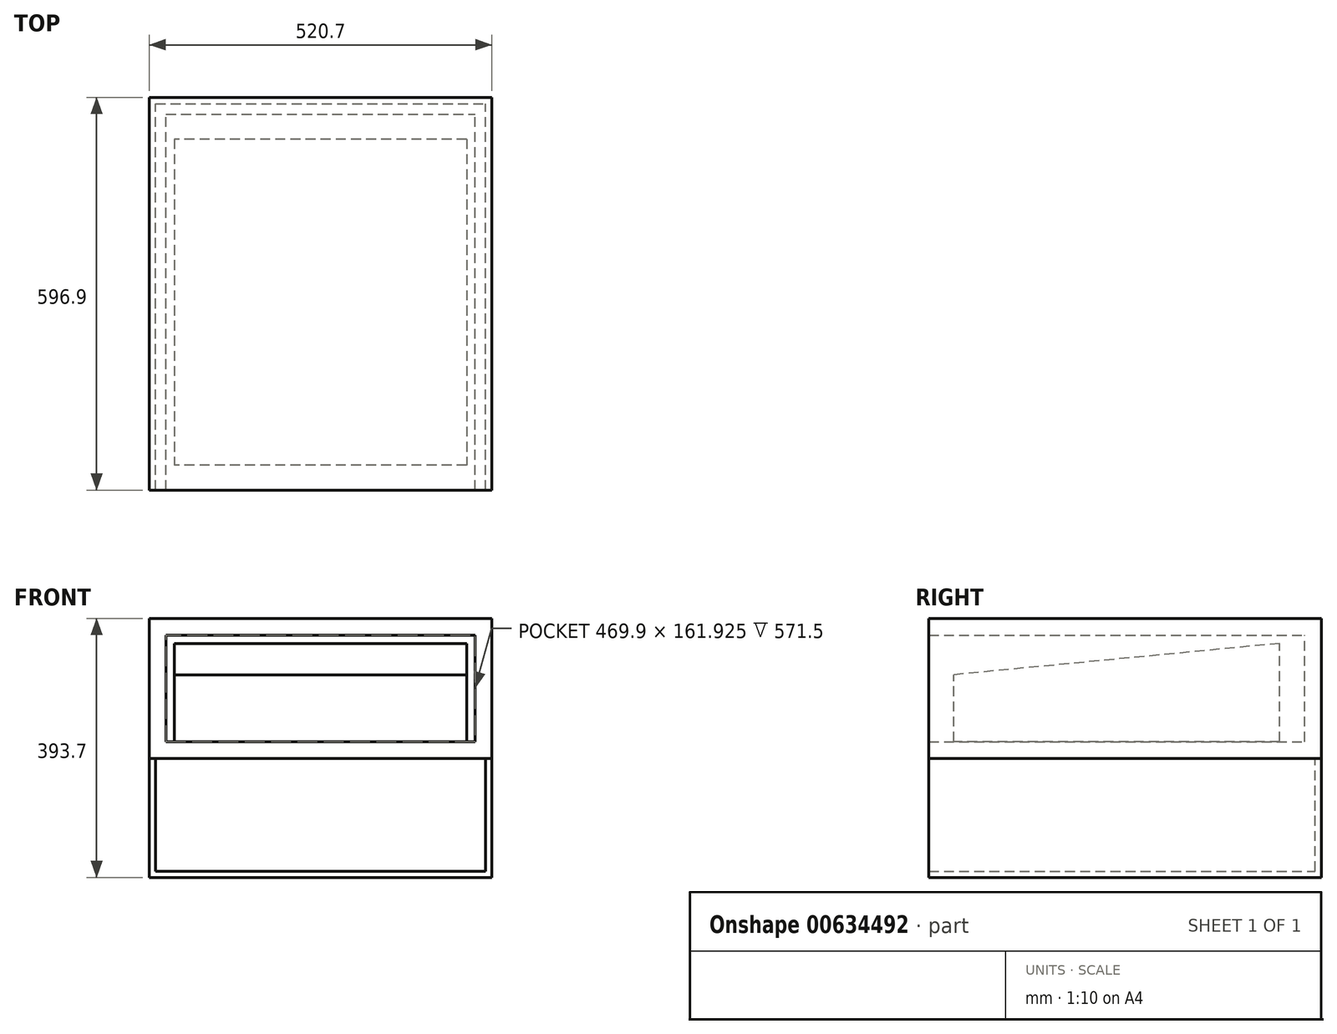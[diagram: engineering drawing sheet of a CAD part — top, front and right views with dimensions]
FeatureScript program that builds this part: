
annotation { "Feature Type Name" : "Feature", "Feature Type Description" : "" }
export const myFeature = defineFeature(function(context is Context, id is Id, definition is map)
    precondition{}
    {
        {
            var Q0;
            Q0=qCreatedBy(makeId("Right.planeOp"),FACE);
            var sketch = newSketch(context, id + "F0", { "sketchPlane" : qUnion([Q0])});
            skLineSegment(sketch, "E0.bottom", {"start": v(0, 0) * mm, "end": v(-495.3, 0) * mm});
            skLineSegment(sketch, "E0.left", {"start": v(0, 0) * mm, "end": v(0, 149.23) * mm});
            skLineSegment(sketch, "E0.right", {"start": v(-495.3, 0) * mm, "end": v(-495.3, 101.6) * mm});
            skLineSegment(sketch, "E1", {"start": v(0, 149.23) * mm, "end": v(-495.3, 101.6) * mm});
            skPoint(sketch, "E2.orphan", {"position": v(-495.3, 203.2) * mm});
            skSolve(sketch);
        }
        {
            var Q0;
            Q0=makeQuery(id+"F0.imprint","IMPRINT",FACE,{"disambiguationData":[TD([[makeQuery(id+"F0.imprint","IMPRINT",EDGE,{"derivedFrom":sQuery(id+"F0.wireOp",EDGE,"E0.bottom")}),-1.0]])]});
            extrude(context, id + "F1", {"entities" : qUnion([Q0]), "depth" : 222.25 * mm, "offsetDistance" : 25.4 * mm, "hasSecondDirection" : true, "secondDirectionOppositeDirection" : true, "secondDirectionDepth" : 222.25 * mm});
        }
        {
            var Q0;
            Q0=makeQuery(id+"F1.opExtrude","SWEPT_FACE",FACE,{"disambiguationData":[OSD([sQuery(id+"F0.wireOp",EDGE,"E0.bottom")])]});
            var sketch = newSketch(context, id + "F2", { "sketchPlane" : qUnion([Q0])});
            skLineSegment(sketch, "E3.0.0", {"start": v(-222.25, 495.3) * mm, "end": v(-222.25, 0) * mm});
            skLineSegment(sketch, "E3.0.1", {"start": v(-222.25, 0) * mm, "end": v(222.25, 0) * mm});
            skLineSegment(sketch, "E3.0.2", {"start": v(222.25, 0) * mm, "end": v(222.25, 495.3) * mm});
            skLineSegment(sketch, "E3.0.3", {"start": v(222.25, 495.3) * mm, "end": v(-222.25, 495.3) * mm});
            skLineSegment(sketch, "E4", {"start": v(0, 495.3) * mm, "end": v(0, 0) * mm, "construction": true});
            skLineSegment(sketch, "E5.bottom", {"start": v(-234.95, 533.4) * mm, "end": v(234.95, 533.4) * mm});
            skLineSegment(sketch, "E5.top", {"start": v(-234.95, -38.1) * mm, "end": v(234.95, -38.1) * mm});
            skLineSegment(sketch, "E5.left", {"start": v(-234.95, 533.4) * mm, "end": v(-234.95, -38.1) * mm});
            skLineSegment(sketch, "E5.right", {"start": v(234.95, 533.4) * mm, "end": v(234.95, -38.1) * mm});
            skPoint(sketch, "E5.middle", {"position": v(0, 247.65) * mm});
            skSolve(sketch);
        }
        {
            var Q0;
            Q0=makeQuery(id+"F2.imprint","IMPRINT",FACE,{"disambiguationData":[TD([[makeQuery(id+"F2.imprint","IMPRINT",EDGE,{"derivedFrom":sQuery(id+"F2.wireOp",EDGE,"E3.0.0")}),1.0]])]});
            var Q1;
            Q1=makeQuery(id+"F2.imprint","IMPRINT",FACE,{"disambiguationData":[TD([[makeQuery(id+"F2.imprint","IMPRINT",EDGE,{"derivedFrom":sQuery(id+"F2.wireOp",EDGE,"E3.0.0")}),-1.0]])]});
            extrude(context, id + "F3", {"entities" : qUnion([Q0, Q1]), "depth" : 25.4 * mm, "offsetDistance" : 25.4 * mm});
        }
        {
            var Q0;
            Q0=makeQuery(id+"F3.opExtrude","SWEPT_FACE",FACE,{"disambiguationData":[OSD([sQuery(id+"F2.wireOp",EDGE,"E5.right")])]});
            var sketch = newSketch(context, id + "F4", { "sketchPlane" : qUnion([Q0])});
            skLineSegment(sketch, "E6.bottom", {"start": v(-533.4, -25.4) * mm, "end": v(38.1, -25.4) * mm});
            skLineSegment(sketch, "E6.top", {"start": v(-533.4, 161.93) * mm, "end": v(38.1, 161.93) * mm});
            skLineSegment(sketch, "E6.left", {"start": v(-533.4, -25.4) * mm, "end": v(-533.4, 161.93) * mm});
            skLineSegment(sketch, "E6.right", {"start": v(38.1, -25.4) * mm, "end": v(38.1, 161.93) * mm});
            skSolve(sketch);
        }
        {
            var Q0;
            {var subQ0=sQuery(id+"F4.wireOp",EDGE,"E6.top");Q0=makeQuery(id+"F4.imprint","IMPRINT",FACE,{"disambiguationData":[TD([[makeQuery(id+"F4.imprint","IMPRINT",EDGE,{"derivedFrom":subQ0}),-1.0]])]});}
            var Q1;
            {var subQ0=sQuery(id+"F4.wireOp",EDGE,"E6.bottom");Q1=makeQuery(id+"F4.imprint","IMPRINT",FACE,{"disambiguationData":[TD([[makeQuery(id+"F4.imprint","IMPRINT",EDGE,{"derivedFrom":subQ0}),1.0]])]});}
            extrude(context, id + "F5", {"entities" : qUnion([Q0, Q1]), "operationType" : NewBodyOperationType.ADD, "depth" : 25.4 * mm, "offsetDistance" : 25.4 * mm});
        }
        {
            var Q0;
            Q0=makeQuery(id+"F3.opExtrude","SWEPT_FACE",FACE,{"disambiguationData":[OSD([sQuery(id+"F2.wireOp",EDGE,"E5.left")])]});
            var sketch = newSketch(context, id + "F6", { "sketchPlane" : qUnion([Q0])});
            skLineSegment(sketch, "E7.0.0", {"start": v(533.4, 161.93) * mm, "end": v(533.4, -25.4) * mm});
            skLineSegment(sketch, "E7.0.1", {"start": v(533.4, -25.4) * mm, "end": v(-38.1, -25.4) * mm});
            skLineSegment(sketch, "E7.0.2", {"start": v(-38.1, -25.4) * mm, "end": v(-38.1, 161.93) * mm});
            skLineSegment(sketch, "E7.0.3", {"start": v(-38.1, 161.93) * mm, "end": v(533.4, 161.93) * mm});
            skSolve(sketch);
        }
        {
            var Q0;
            {var subQ2=sQuery(id+"F6.wireOp",EDGE,"E7.0.3");Q0=makeQuery(id+"F6.imprint","IMPRINT",FACE,{"disambiguationData":[TD([[makeQuery(id+"F6.imprint","IMPRINT",EDGE,{"derivedFrom":subQ2}),-1.0]])]});}
            var Q1;
            {var subQ2=sQuery(id+"F6.wireOp",EDGE,"E7.0.1");Q1=makeQuery(id+"F6.imprint","IMPRINT",FACE,{"disambiguationData":[TD([[makeQuery(id+"F6.imprint","IMPRINT",EDGE,{"derivedFrom":subQ2}),-1.0]])]});}
            extrude(context, id + "F7", {"entities" : qUnion([Q0, Q1]), "operationType" : NewBodyOperationType.ADD, "depth" : 25.4 * mm, "offsetDistance" : 25.4 * mm});
        }
        {
            var Q0;
            Q0=makeQuery(id+"F7.boolean.opBoolean","MERGE",FACE,{"derivedFrom":[makeQuery(id+"F5.boolean.opBoolean","MERGE",FACE,{"derivedFrom":[makeQuery(id+"F3.opExtrude","SWEPT_FACE",FACE,{"disambiguationData":[OSD([sQuery(id+"F2.wireOp",EDGE,"E5.top")])]}),makeQuery(id+"F5.opExtrude","SWEPT_FACE",FACE,{"disambiguationData":[OSD([sQuery(id+"F4.wireOp",EDGE,"E6.right")])]})]}),makeQuery(id+"F7.opExtrude","SWEPT_FACE",FACE,{"disambiguationData":[OSD([sQuery(id+"F6.wireOp",EDGE,"E7.0.2")])]})]});
            var sketch = newSketch(context, id + "F8", { "sketchPlane" : qUnion([Q0])});
            skLineSegment(sketch, "E8.bottom", {"start": v(-260.35, -25.4) * mm, "end": v(260.35, -25.4) * mm});
            skLineSegment(sketch, "E8.top", {"start": v(-260.35, 161.93) * mm, "end": v(260.35, 161.93) * mm});
            skLineSegment(sketch, "E8.left", {"start": v(-260.35, -25.4) * mm, "end": v(-260.35, 161.93) * mm});
            skLineSegment(sketch, "E8.right", {"start": v(260.35, -25.4) * mm, "end": v(260.35, 161.93) * mm});
            skSolve(sketch);
        }
        {
            var Q0;
            Q0=makeQuery(id+"F8.imprint","IMPRINT",FACE,{"disambiguationData":[TD([[makeQuery(id+"F8.imprint","IMPRINT",EDGE,{"derivedFrom":makeQuery(id+"F3.opExtrude","CAP_EDGE",EDGE,{"disambiguationData":[OSD([sQuery(id+"F2.wireOp",EDGE,"E5.top")])],"isStart":true})}),-1.0]])]});
            var Q1;
            Q1=makeQuery(id+"F8.imprint","IMPRINT",FACE,{"disambiguationData":[TD([[makeQuery(id+"F8.imprint","IMPRINT",EDGE,{"derivedFrom":sQuery(id+"F8.wireOp",EDGE,"E8.bottom")}),-1.0]])]});
            extrude(context, id + "F9", {"entities" : qUnion([Q0, Q1]), "operationType" : NewBodyOperationType.ADD, "depth" : 25.4 * mm, "offsetDistance" : 25.4 * mm});
        }
        {
            var Q0;
            Q0=makeQuery(id+"F9.boolean.opBoolean","MERGE",FACE,{"derivedFrom":[makeQuery(id+"F5.opExtrude","SWEPT_FACE",FACE,{"disambiguationData":[OSD([sQuery(id+"F4.wireOp",EDGE,"E6.top")])]}),makeQuery(id+"F7.opExtrude","SWEPT_FACE",FACE,{"disambiguationData":[OSD([sQuery(id+"F6.wireOp",EDGE,"E7.0.3")])]}),makeQuery(id+"F9.opExtrude","SWEPT_FACE",FACE,{"disambiguationData":[OSD([sQuery(id+"F8.wireOp",EDGE,"E8.top")])]})]});
            var sketch = newSketch(context, id + "F10", { "sketchPlane" : qUnion([Q0])});
            skLineSegment(sketch, "E9.bottom", {"start": v(260.35, -533.4) * mm, "end": v(-260.35, -533.4) * mm});
            skLineSegment(sketch, "E9.top", {"start": v(260.35, 63.5) * mm, "end": v(-260.35, 63.5) * mm});
            skLineSegment(sketch, "E9.left", {"start": v(260.35, -533.4) * mm, "end": v(260.35, 63.5) * mm});
            skLineSegment(sketch, "E9.right", {"start": v(-260.35, -533.4) * mm, "end": v(-260.35, 63.5) * mm});
            skSolve(sketch);
        }
        {
            var Q0;
            Q0=makeQuery(id+"F10.imprint","IMPRINT",FACE,{"disambiguationData":[TD([[makeQuery(id+"F10.imprint","IMPRINT",EDGE,{"derivedFrom":sQuery(id+"F10.wireOp",EDGE,"E9.top")}),1.0]])]});
            var Q1;
            {var subQ1=makeQuery(id+"F5.opExtrude","CAP_EDGE",EDGE,{"disambiguationData":[OSD([sQuery(id+"F4.wireOp",EDGE,"E6.top")])],"isStart":true});Q1=makeQuery(id+"F10.imprint","IMPRINT",FACE,{"disambiguationData":[TD([[makeQuery(id+"F10.imprint","IMPRINT",EDGE,{"derivedFrom":subQ1}),1.0]])]});}
            extrude(context, id + "F11", {"entities" : qUnion([Q0, Q1]), "operationType" : NewBodyOperationType.ADD, "depth" : 25.4 * mm, "offsetDistance" : 25.4 * mm});
        }
        {
            var Q0;
            Q0=makeQuery(id+"F9.boolean.opBoolean","MERGE",FACE,{"derivedFrom":[makeQuery(id+"F7.boolean.opBoolean","MERGE",FACE,{"derivedFrom":[makeQuery(id+"F5.boolean.opBoolean","MERGE",FACE,{"derivedFrom":[makeQuery(id+"F3.opExtrude","CAP_FACE",FACE,{"disambiguationData":[OSD([sQuery(id+"F2.wireOp",EDGE,"E5.bottom"),sQuery(id+"F2.wireOp",EDGE,"E5.top"),sQuery(id+"F2.wireOp",EDGE,"E5.left"),sQuery(id+"F2.wireOp",EDGE,"E5.right")])],"isStart":false}),makeQuery(id+"F5.opExtrude","SWEPT_FACE",FACE,{"disambiguationData":[OSD([sQuery(id+"F4.wireOp",EDGE,"E6.bottom")])]})]}),makeQuery(id+"F7.opExtrude","SWEPT_FACE",FACE,{"disambiguationData":[OSD([sQuery(id+"F6.wireOp",EDGE,"E7.0.1")])]})]}),makeQuery(id+"F9.opExtrude","SWEPT_FACE",FACE,{"disambiguationData":[OSD([sQuery(id+"F8.wireOp",EDGE,"E8.bottom")])]})]});
            var sketch = newSketch(context, id + "F12", { "sketchPlane" : qUnion([Q0])});
            skLineSegment(sketch, "E10.0.0", {"start": v(260.35, 533.4) * mm, "end": v(-260.35, 533.4) * mm});
            skLineSegment(sketch, "E10.0.1", {"start": v(-260.35, 533.4) * mm, "end": v(-260.35, -63.5) * mm});
            skLineSegment(sketch, "E10.0.2", {"start": v(-260.35, -63.5) * mm, "end": v(260.35, -63.5) * mm});
            skLineSegment(sketch, "E10.0.3", {"start": v(260.35, -63.5) * mm, "end": v(260.35, 533.4) * mm});
            skLineSegment(sketch, "E11", {"start": v(0, 533.4) * mm, "end": v(0, -63.5) * mm, "construction": true});
            skLineSegment(sketch, "E12.bottom", {"start": v(-250.83, 523.88) * mm, "end": v(250.83, 523.88) * mm});
            skLineSegment(sketch, "E12.top", {"start": v(-250.83, -53.97) * mm, "end": v(250.83, -53.97) * mm});
            skLineSegment(sketch, "E12.left", {"start": v(-250.83, 523.88) * mm, "end": v(-250.83, -53.97) * mm});
            skLineSegment(sketch, "E12.right", {"start": v(250.83, 523.88) * mm, "end": v(250.83, -53.97) * mm});
            skPoint(sketch, "E12.middle", {"position": v(0, 234.95) * mm});
            skLineSegment(sketch, "E13", {"start": v(-250.83, 523.88) * mm, "end": v(-250.83, 533.4) * mm});
            skLineSegment(sketch, "E14", {"start": v(-250.83, -53.97) * mm, "end": v(-250.83, -63.5) * mm});
            skLineSegment(sketch, "E15", {"start": v(250.83, -53.97) * mm, "end": v(250.83, -63.5) * mm});
            skLineSegment(sketch, "E16", {"start": v(250.83, 523.88) * mm, "end": v(250.83, 533.4) * mm});
            skSolve(sketch);
        }
        {
            var Q0;
            {var subQ0=sQuery(id+"F12.wireOp",EDGE,"E10.0.3");Q0=makeQuery(id+"F12.imprint","IMPRINT",FACE,{"disambiguationData":[TD([[makeQuery(id+"F12.imprint","IMPRINT",EDGE,{"derivedFrom":subQ0}),-1.0]])]});}
            var Q1;
            Q1=makeQuery(id+"F12.imprint","IMPRINT",FACE,{"disambiguationData":[TD([[makeQuery(id+"F12.imprint","IMPRINT",EDGE,{"derivedFrom":sQuery(id+"F12.wireOp",EDGE,"E12.top")}),-1.0]])]});
            var Q2;
            {var subQ1=sQuery(id+"F12.wireOp",EDGE,"E10.0.1");Q2=makeQuery(id+"F12.imprint","IMPRINT",FACE,{"disambiguationData":[TD([[makeQuery(id+"F12.imprint","IMPRINT",EDGE,{"derivedFrom":subQ1}),1.0]])]});}
            extrude(context, id + "F13", {"entities" : qUnion([Q0, Q1, Q2]), "depth" : 171.45 * mm, "offsetDistance" : 25.4 * mm});
        }
        {
            var Q0;
            Q0=makeQuery(id+"F13.opExtrude","CAP_FACE",FACE,{"disambiguationData":[OSD([sQuery(id+"F12.wireOp",EDGE,"E10.0.0"),sQuery(id+"F12.wireOp",EDGE,"E10.0.1"),sQuery(id+"F12.wireOp",EDGE,"E10.0.2"),sQuery(id+"F12.wireOp",EDGE,"E10.0.3"),sQuery(id+"F12.wireOp",EDGE,"E12.top"),sQuery(id+"F12.wireOp",EDGE,"E12.left"),sQuery(id+"F12.wireOp",EDGE,"E12.right"),sQuery(id+"F12.wireOp",EDGE,"E13"),sQuery(id+"F12.wireOp",EDGE,"E16")])],"isStart":false});
            var sketch = newSketch(context, id + "F14", { "sketchPlane" : qUnion([Q0])});
            skLineSegment(sketch, "E17.bottom", {"start": v(-260.35, -63.5) * mm, "end": v(260.35, -63.5) * mm});
            skLineSegment(sketch, "E17.top", {"start": v(-260.35, 533.4) * mm, "end": v(260.35, 533.4) * mm});
            skLineSegment(sketch, "E17.left", {"start": v(-260.35, -63.5) * mm, "end": v(-260.35, 533.4) * mm});
            skLineSegment(sketch, "E17.right", {"start": v(260.35, -63.5) * mm, "end": v(260.35, 533.4) * mm});
            skSolve(sketch);
        }
        {
            var Q0;
            Q0=makeQuery(id+"F14.imprint","IMPRINT",FACE,{"disambiguationData":[TD([[makeQuery(id+"F14.imprint","IMPRINT",EDGE,{"derivedFrom":makeQuery(id+"F13.opExtrude","CAP_EDGE",EDGE,{"disambiguationData":[OSD([sQuery(id+"F12.wireOp",EDGE,"E12.top")])],"isStart":false})}),1.0]])]});
            var Q1;
            Q1=makeQuery(id+"F14.imprint","IMPRINT",FACE,{"disambiguationData":[TD([[makeQuery(id+"F14.imprint","IMPRINT",EDGE,{"derivedFrom":sQuery(id+"F14.wireOp",EDGE,"E17.bottom")}),1.0]])]});
            extrude(context, id + "F15", {"entities" : qUnion([Q0, Q1]), "operationType" : NewBodyOperationType.ADD, "depth" : 9.52 * mm, "offsetDistance" : 25.4 * mm});
        }
    });
